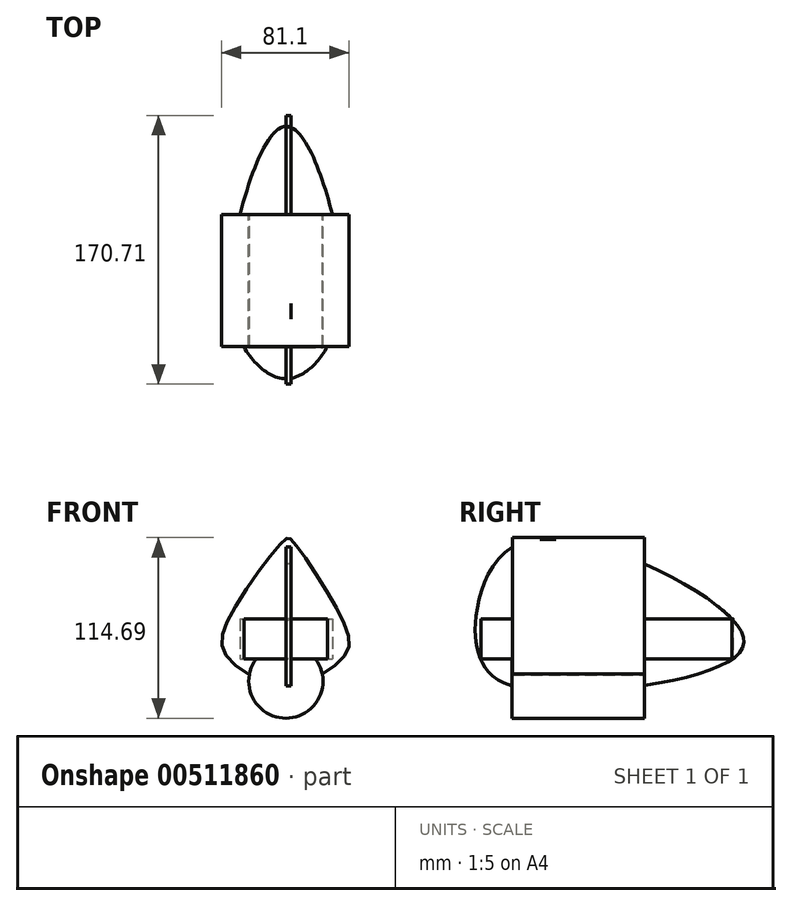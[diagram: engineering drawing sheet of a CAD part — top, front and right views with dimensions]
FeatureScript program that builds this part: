
annotation { "Feature Type Name" : "Feature", "Feature Type Description" : "" }
export const myFeature = defineFeature(function(context is Context, id is Id, definition is map)
    precondition{}
    {
        {
            var Q0;
            Q0=qCreatedBy(makeId("Top.planeOp"),FACE);
            var sketch = newSketch(context, id + "F0", { "sketchPlane" : qUnion([Q0])});
            skLineSegment(sketch, "E0.bottom", {"start": v(29.48, 0) * mm, "end": v(-29.93, 0) * mm});
            skLineSegment(sketch, "E0.top", {"start": v(29.48, -77.42) * mm, "end": v(-29.93, -77.42) * mm});
            skLineSegment(sketch, "E0.left", {"start": v(29.48, 0) * mm, "end": v(29.48, -77.42) * mm});
            skLineSegment(sketch, "E0.right", {"start": v(-29.93, 0) * mm, "end": v(-29.93, -77.42) * mm});
            skFitSpline(sketch, "E1", {"points": [v(-29.93, -3.26) * mm, v(0, 56.15) * mm, v(29.48, 0) * mm, v(29.48, -77.42) * mm, v(0, -104.22) * mm, v(-29.93, -77.42) * mm, v(-29.93, -3.26) * mm]});
            skSolve(sketch);
        }
        {
            var Q0;
            Q0 = qSketchRegion(id + "F0", true);
            extrude(context, id + "F1", {"entities" : qUnion([Q0]), "depth" : 25.4 * mm});
        }
        {
            var Q0;
            Q0=qCreatedBy(makeId("Right.planeOp"),FACE);
            var sketch = newSketch(context, id + "F2", { "sketchPlane" : qUnion([Q0])});
            skFitSpline(sketch, "E2", {"points": [v(-106.94, 27.91) * mm, v(-75.03, 74.6) * mm, v(55.51, 25.37) * mm, v(56, 0) * mm, v(-78.9, -18.54) * mm, v(-104.26, 0) * mm, v(-106.94, 27.91) * mm]});
            skSolve(sketch);
        }
        {
            var Q0;
            Q0=qCreatedBy(makeId("Front.planeOp"),FACE);
            var sketch = newSketch(context, id + "F3", { "sketchPlane" : qUnion([Q0])});
            skFitSpline(sketch, "E3", {"points": [v(3.66, -20.25) * mm, v(35.86, 0) * mm, v(35.86, 24.88) * mm, v(3.66, 75.62) * mm, v(0, 76.35) * mm, v(-36.1, 25.86) * mm, v(-36.1, 0) * mm, v(0, -21.47) * mm, v(3.66, -20.25) * mm]});
            skSolve(sketch);
        }
        {
            var Q0;
            Q0=qCreatedBy(makeId("Front.planeOp"),FACE);
            var sketch = newSketch(context, id + "F4", { "sketchPlane" : qUnion([Q0])});
            skCircle(sketch, "E4", {"center": v(0, -14.09) * mm, "radius": 23.56 * mm});
            skSolve(sketch);
        }
        {
            var Q0;
            Q0=makeQuery(id+"F2.imprint","IMPRINT",FACE,{"disambiguationData":[TD([[makeQuery(id+"F2.imprint","IMPRINT",EDGE,{"derivedFrom":sQuery(id+"F2.wireOp",EDGE,"E2")}),-1.0]])]});
            extrude(context, id + "F5", {"entities" : qUnion([Q0]), "operationType" : NewBodyOperationType.ADD, "depth" : 3.3 * mm});
        }
        {
            var Q0;
            Q0=makeQuery(id+"F3.imprint","IMPRINT",FACE,{"disambiguationData":[TD([[makeQuery(id+"F3.imprint","IMPRINT",EDGE,{"derivedFrom":sQuery(id+"F3.wireOp",EDGE,"E3")}),1.0]])]});
            extrude(context, id + "F6", {"entities" : qUnion([Q0]), "operationType" : NewBodyOperationType.ADD, "depth" : 83.82 * mm});
        }
        {
            var Q0;
            Q0=makeQuery(id+"F4.imprint","IMPRINT",FACE,{"disambiguationData":[TD([[makeQuery(id+"F4.imprint","IMPRINT",EDGE,{"derivedFrom":sQuery(id+"F4.wireOp",EDGE,"E4")}),1.0]])]});
            extrude(context, id + "F7", {"entities" : qUnion([Q0]), "operationType" : NewBodyOperationType.ADD, "depth" : 84.33 * mm});
        }
        {
            var Q0;
            Q0=qCreatedBy(makeId("Right.planeOp"),FACE);
            var sketch = newSketch(context, id + "F8", { "sketchPlane" : qUnion([Q0])});
            skFitSpline(sketch, "E5", {"points": [v(67.63, 11.4) * mm, v(0, -37.24) * mm, v(-83.7, -37.83) * mm, v(-104.8, 0) * mm, v(0, 0) * mm, v(59.62, 20.5) * mm, v(67.63, 11.4) * mm]});
            skSolve(sketch);
        }
        {
            var Q0;
            Q0=sQuery(id+"F8.wireOp",EDGE,"E5");
            extrude(context, id + "F9", {"bodyType" : ToolBodyType.SURFACE, "surfaceEntities" : qUnion([Q0]), "depth" : 2.8 * mm});
        }
    });
